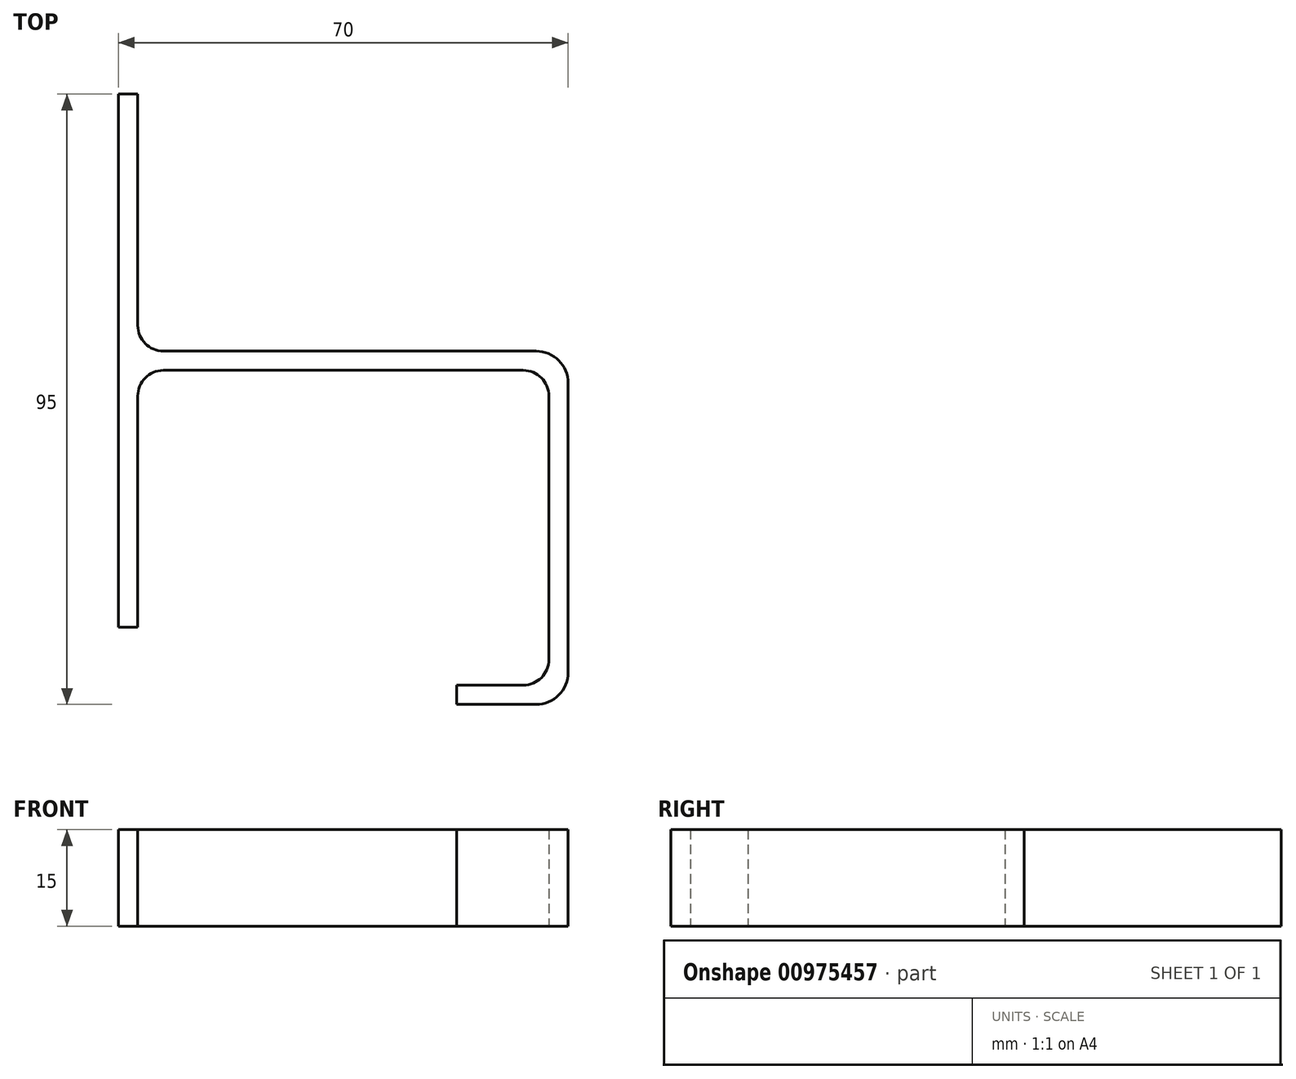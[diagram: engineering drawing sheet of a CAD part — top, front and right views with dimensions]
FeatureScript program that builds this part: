
annotation { "Feature Type Name" : "Feature", "Feature Type Description" : "" }
export const myFeature = defineFeature(function(context is Context, id is Id, definition is map)
    precondition{}
    {
        {
            var Q0;
            Q0=qCreatedBy(makeId("Top.planeOp"),FACE);
            var sketch = newSketch(context, id + "F0", { "sketchPlane" : qUnion([Q0])});
            skLineSegment(sketch, "E0", {"start": v(0, -43) * mm, "end": v(3, -43) * mm});
            skLineSegment(sketch, "E1", {"start": v(70, -5) * mm, "end": v(70, -50) * mm});
            skLineSegment(sketch, "E2", {"start": v(65, -55) * mm, "end": v(52.67, -55) * mm});
            skLineSegment(sketch, "E3", {"start": v(52.67, -55) * mm, "end": v(52.67, -52) * mm});
            skLineSegment(sketch, "E4", {"start": v(52.67, -52) * mm, "end": v(63, -52) * mm});
            skLineSegment(sketch, "E5", {"start": v(67, -48) * mm, "end": v(67, -7) * mm});
            skLineSegment(sketch, "E6", {"start": v(63, -3) * mm, "end": v(7, -3) * mm});
            skLineSegment(sketch, "E7", {"start": v(3, -7) * mm, "end": v(3, -43) * mm});
            skPoint(sketch, "E8.visualSharp", {"position": v(70, -55) * mm});
            skLineSegment(sketch, "E8.filletArc", {"start": v(70, -55) * mm, "end": v(70, -55) * mm});
            skPoint(sketch, "E9.visualSharp", {"position": v(67, -3) * mm});
            skLineSegment(sketch, "E9.filletArc", {"start": v(67, -3) * mm, "end": v(67, -3) * mm});
            skPoint(sketch, "E10.visualSharp", {"position": v(70, 0) * mm});
            skLineSegment(sketch, "E10.filletArc", {"start": v(70, 0) * mm, "end": v(70, 0) * mm});
            skPoint(sketch, "E11.visualSharp", {"position": v(67, -52) * mm});
            skArc(sketch, "E11.filletArc", {"start": v(63, -52) * mm, "mid": v(65.83, -50.83) * mm, "end": v(67, -48) * mm});
            skArc(sketch, "E12.filletArc", {"start": v(67, -7) * mm, "mid": v(65.83, -4.17) * mm, "end": v(63, -3) * mm});
            skArc(sketch, "E13.filletArc", {"start": v(65, -55) * mm, "mid": v(68.54, -53.54) * mm, "end": v(70, -50) * mm});
            skArc(sketch, "E14.filletArc", {"start": v(70, -5) * mm, "mid": v(68.54, -1.46) * mm, "end": v(65, 0) * mm});
            skLineSegment(sketch, "E15", {"start": v(65, 0) * mm, "end": v(7, 0) * mm});
            skLineSegment(sketch, "E16", {"start": v(3, 4) * mm, "end": v(3, 40) * mm});
            skLineSegment(sketch, "E17", {"start": v(0, -43) * mm, "end": v(0, 40) * mm});
            skLineSegment(sketch, "E18", {"start": v(0, 40) * mm, "end": v(3, 40) * mm});
            skPoint(sketch, "E19.visualSharp", {"position": v(3, 0) * mm});
            skArc(sketch, "E19.filletArc", {"start": v(3, 4) * mm, "mid": v(4.17, 1.17) * mm, "end": v(7, 0) * mm});
            skPoint(sketch, "E20.visualSharp", {"position": v(3, -3) * mm});
            skArc(sketch, "E20.filletArc", {"start": v(7, -3) * mm, "mid": v(4.17, -4.17) * mm, "end": v(3, -7) * mm});
            skSolve(sketch);
        }
        {
            var Q0;
            Q0=makeQuery(id+"F0.imprint","IMPRINT",FACE,{"disambiguationData":[TD([[makeQuery(id+"F0.imprint","IMPRINT",EDGE,{"derivedFrom":sQuery(id+"F0.wireOp",EDGE,"E0")}),1.0]])]});
            extrude(context, id + "F1", {"entities" : qUnion([Q0]), "depth" : 15 * mm, "offsetDistance" : 25 * mm});
        }
    });
